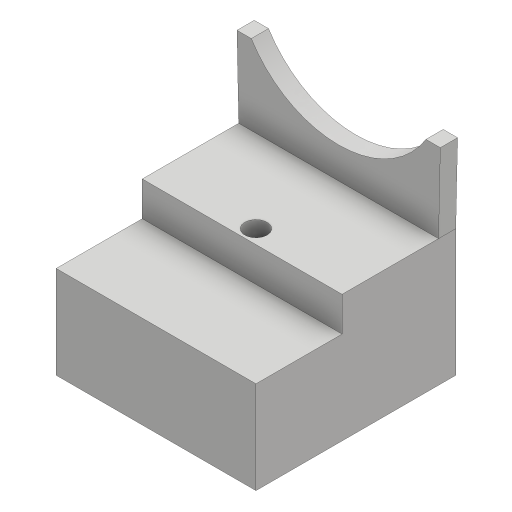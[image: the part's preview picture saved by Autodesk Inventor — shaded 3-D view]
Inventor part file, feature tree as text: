
AUTODESK INVENTOR PART (.ipt)
format: ipt  version: 2023 (Build 270158000, 158)  size: 134,656 bytes
history: native  units: mm
features: sketch x3, extrude x3, hole x1, projected_geometry x1
ambient origin geometry x8: Origin, YZ Plane, XZ Plane, XY Plane, X Axis, Y Axis, Z Axis, Center Point
bodies: Solid1 (feature_tree)
feature tree (8):
  sketch  "Sketch1"  dims[d0=58.0mm d1=58.0mm]
  extrude  "Extrusion1"  Depth=58.0mm
  extrude  "Extrusion2"  Depth=10.0mm TaperAngle=0.0deg
  hole  "Hole1"  [1 undecoded]
  extrude  "Extrusion3"  Depth=5.0mm TaperAngle=0.0deg
  sketch  "Sketch2"  dims[d2=36.866mm d3=0.0mm d4=10.0mm d5=0.0mm]
  sketch  "Sketch3"  dims[d6=6.5mm d7=6.0mm d8=4.0mm d9=2.0mm d10=90.0deg d11=8.0mm d12=20.594885mm d13=59.75mm d14=5.0mm d15=0.0mm]
  projected_geometry  "Projected Loop1"
note: 1 required parameter value undecoded (feature->parameter linkage not recoverable at this tier; creation-order binding heuristic only, values carry confidence <= 0.55)
